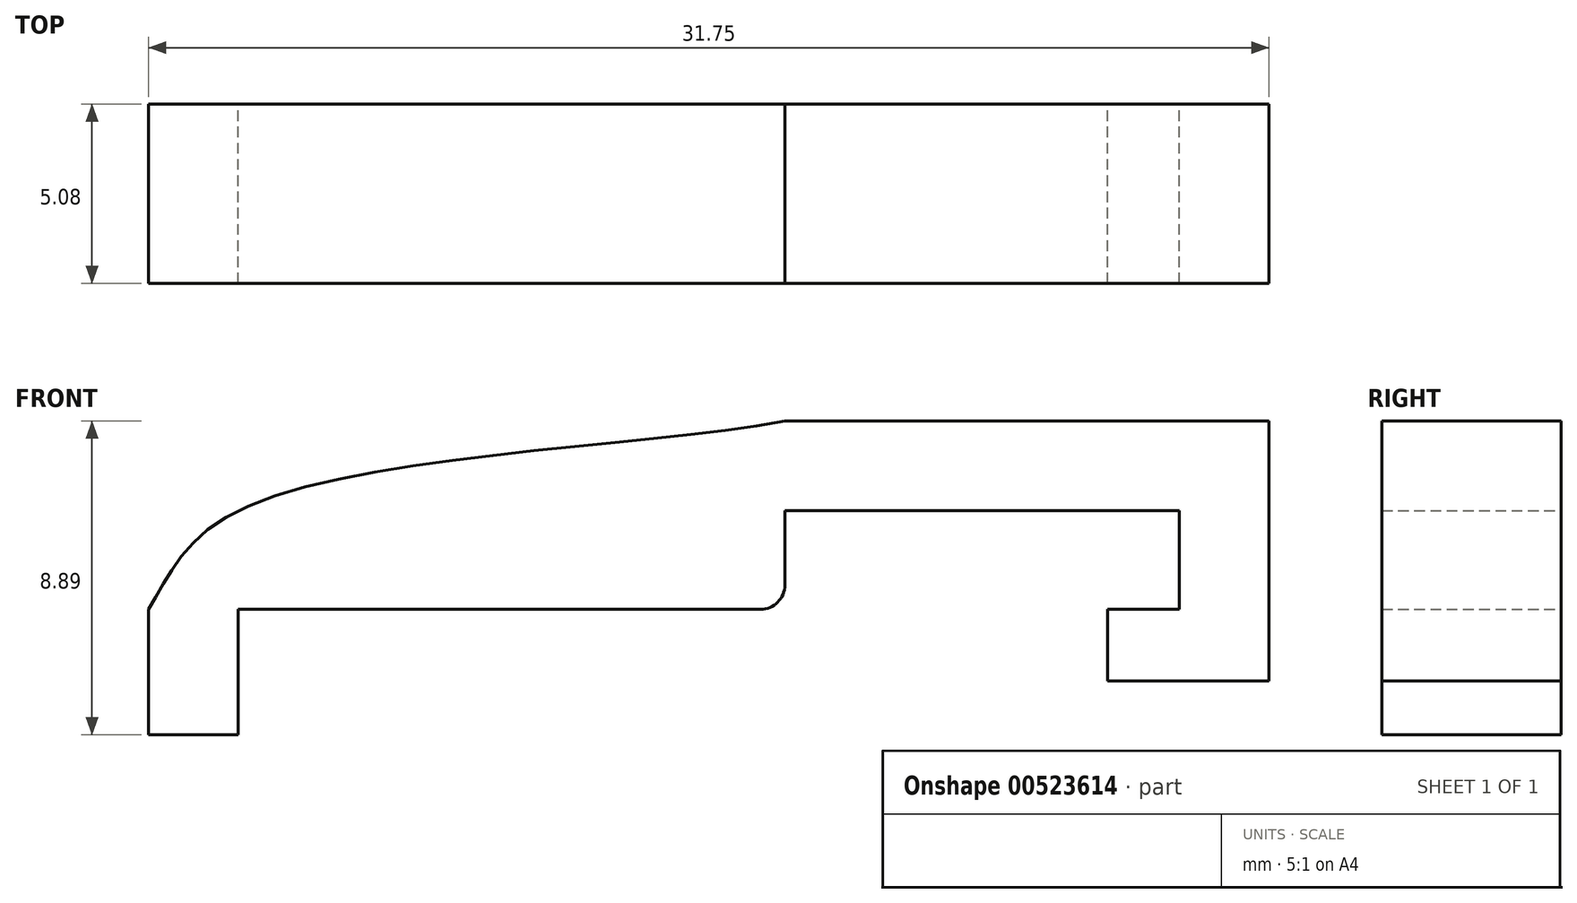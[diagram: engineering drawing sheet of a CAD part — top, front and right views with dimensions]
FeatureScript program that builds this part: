
annotation { "Feature Type Name" : "Feature", "Feature Type Description" : "" }
export const myFeature = defineFeature(function(context is Context, id is Id, definition is map)
    precondition{}
    {
        {
            var Q0;
            Q0=qCreatedBy(makeId("Front.planeOp"),FACE);
            var sketch = newSketch(context, id + "F0", { "sketchPlane" : qUnion([Q0])});
            skLineSegment(sketch, "E0", {"start": v(-0.89, 5.67) * mm, "end": v(10.29, 5.67) * mm});
            skLineSegment(sketch, "E1", {"start": v(10.29, 5.67) * mm, "end": v(10.29, 2.87) * mm});
            skLineSegment(sketch, "E2", {"start": v(10.29, 2.87) * mm, "end": v(8.26, 2.87) * mm});
            skLineSegment(sketch, "E3", {"start": v(8.26, 2.87) * mm, "end": v(8.26, 0.84) * mm});
            skLineSegment(sketch, "E4", {"start": v(8.26, 0.84) * mm, "end": v(12.83, 0.84) * mm});
            skLineSegment(sketch, "E5", {"start": v(12.83, 0.84) * mm, "end": v(12.83, 8.2) * mm});
            skLineSegment(sketch, "E6", {"start": v(12.83, 8.2) * mm, "end": v(-0.89, 8.2) * mm});
            skLineSegment(sketch, "E7", {"start": v(-18.92, 2.87) * mm, "end": v(-18.92, -0.68) * mm});
            skLineSegment(sketch, "E8", {"start": v(-18.92, -0.68) * mm, "end": v(-16.38, -0.68) * mm});
            skLineSegment(sketch, "E9", {"start": v(-16.38, -0.68) * mm, "end": v(-16.38, 2.87) * mm});
            skLineSegment(sketch, "E10", {"start": v(-0.89, 5.67) * mm, "end": v(-0.89, 3.56) * mm});
            skLineSegment(sketch, "E11", {"start": v(-1.58, 2.87) * mm, "end": v(-16.38, 2.87) * mm});
            skPoint(sketch, "E12.orphan", {"position": v(-16.38, 5.67) * mm});
            skFitSpline(sketch, "E13", {"points": [v(-18.92, 2.87) * mm, v(-16.38, 5.67) * mm, v(-0.89, 8.2) * mm], "startDerivative": vector(4.94, 7.75) * mm, "endDerivative": vector(17, 3.25) * mm});
            skPoint(sketch, "E14.visualSharp", {"position": v(-0.89, 2.87) * mm});
            skArc(sketch, "E14.filletArc", {"start": v(-1.58, 2.87) * mm, "mid": v(-1.1, 3.08) * mm, "end": v(-0.89, 3.56) * mm});
            skLineSegment(sketch, "E15", {"start": v(-16.38, 2.87) * mm, "end": v(-18.92, 2.87) * mm, "construction": true});
            skLineSegment(sketch, "E16", {"start": v(-1.58, 2.87) * mm, "end": v(8.26, 2.87) * mm, "construction": true});
            skSolve(sketch);
        }
        {
            var Q0;
            Q0 = qSketchRegion(id + "F0", true);
            extrude(context, id + "F1", {"entities" : qUnion([Q0]), "depth" : 5.08 * mm, "offsetDistance" : 25.4 * mm});
        }
    });
